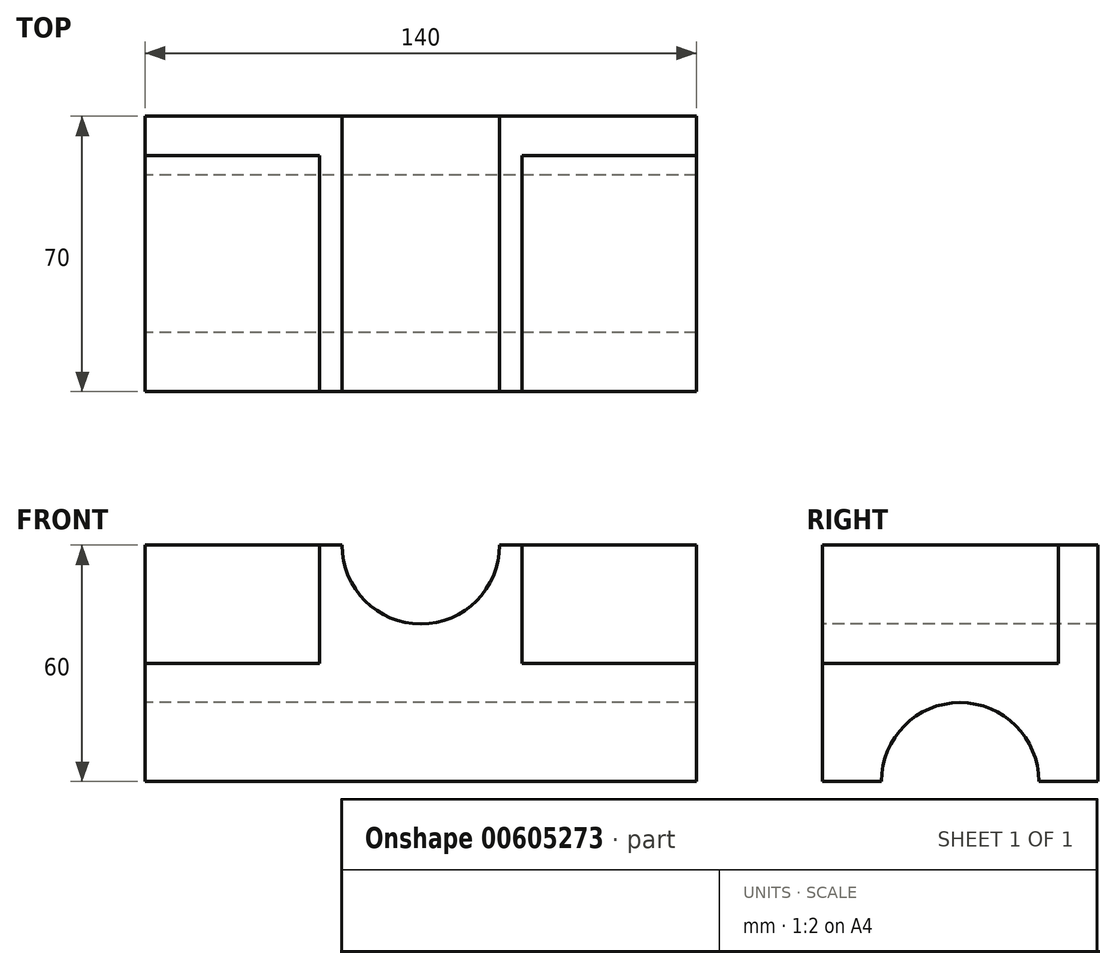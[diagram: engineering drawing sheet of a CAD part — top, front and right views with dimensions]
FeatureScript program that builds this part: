
annotation { "Feature Type Name" : "Feature", "Feature Type Description" : "" }
export const myFeature = defineFeature(function(context is Context, id is Id, definition is map)
    precondition{}
    {
        {
            var Q0;
            Q0=qCreatedBy(makeId("Right.planeOp"),FACE);
            var sketch = newSketch(context, id + "F0", { "sketchPlane" : qUnion([Q0])});
            skLineSegment(sketch, "E0", {"start": v(0, 30) * mm, "end": v(0, 0) * mm});
            skLineSegment(sketch, "E1", {"start": v(0, 0) * mm, "end": v(-60, 0) * mm});
            skLineSegment(sketch, "E2", {"start": v(-60, 0) * mm, "end": v(-60, -30) * mm});
            skLineSegment(sketch, "E3", {"start": v(-60, -30) * mm, "end": v(10, -30) * mm, "construction": true});
            skLineSegment(sketch, "E4", {"start": v(10, -30) * mm, "end": v(10, 30) * mm});
            skLineSegment(sketch, "E5", {"start": v(10, 30) * mm, "end": v(0, 30) * mm});
            skArc(sketch, "E6", {"start": v(-45, -30) * mm, "mid": v(-25, -10) * mm, "end": v(-5, -30) * mm});
            skLineSegment(sketch, "E7", {"start": v(-5, -30) * mm, "end": v(0, -30) * mm});
            skLineSegment(sketch, "E8", {"start": v(-60, -30) * mm, "end": v(-45, -30) * mm});
            skLineSegment(sketch, "E9", {"start": v(-5, -30) * mm, "end": v(10, -30) * mm});
            skSolve(sketch);
        }
        {
            var Q0;
            Q0 = qSketchRegion(id + "F0", true);
            extrude(context, id + "F1", {"entities" : qUnion([Q0]), "endBound" : BoundingType.SYMMETRIC, "depth" : 140 * mm, "offsetDistance" : 25 * mm});
        }
        {
            var Q0;
            Q0=makeQuery(id+"F1.opExtrude","SWEPT_FACE",FACE,{"disambiguationData":[OSD([sQuery(id+"F0.wireOp",EDGE,"E0")])]});
            var sketch = newSketch(context, id + "F2", { "sketchPlane" : qUnion([Q0])});
            skLineSegment(sketch, "E10.bottom", {"start": v(25.7, 0) * mm, "end": v(0, 0) * mm});
            skLineSegment(sketch, "E10.top", {"start": v(25.7, 30) * mm, "end": v(0, 30) * mm});
            skLineSegment(sketch, "E10.left", {"start": v(25.7, 0) * mm, "end": v(25.7, 30) * mm});
            skLineSegment(sketch, "E10.right", {"start": v(0, 0) * mm, "end": v(0, 30) * mm});
            skSolve(sketch);
        }
        {
            var Q0;
            Q0 = qSketchRegion(id + "F2", true);
            extrude(context, id + "F3", {"entities" : qUnion([Q0]), "operationType" : NewBodyOperationType.ADD, "depth" : 60 * mm, "offsetDistance" : 25 * mm});
        }
        {
            var Q0;
            Q0=makeQuery(id+"F1.opExtrude","SWEPT_BODY",BODY,{"disambiguationData":[OSD([sQuery(id+"F0.wireOp",EDGE,"E0"),sQuery(id+"F0.wireOp",EDGE,"E1"),sQuery(id+"F0.wireOp",EDGE,"E2"),sQuery(id+"F0.wireOp",EDGE,"E4"),sQuery(id+"F0.wireOp",EDGE,"E5"),sQuery(id+"F0.wireOp",EDGE,"E6"),sQuery(id+"F0.wireOp",EDGE,"E8"),sQuery(id+"F0.wireOp",EDGE,"E9")])]});
            var Q1;
            Q1=qCreatedBy(makeId("Right.planeOp"),FACE);
            mirror(context, id + "F4", {"operationType" : NewBodyOperationType.ADD, "entities" : qUnion([Q0]), "mirrorPlane" : qUnion([Q1])});
        }
        {
            var Q0;
            {var subQ0=makeQuery(id+"F3.boolean.opBoolean","MERGE",FACE,{"derivedFrom":[makeQuery(id+"F1.opExtrude","SWEPT_FACE",FACE,{"disambiguationData":[OSD([sQuery(id+"F0.wireOp",EDGE,"E2")])]}),makeQuery(id+"F3.opExtrude","CAP_FACE",FACE,{"disambiguationData":[OSD([sQuery(id+"F2.wireOp",EDGE,"E10.bottom"),sQuery(id+"F2.wireOp",EDGE,"E10.top"),sQuery(id+"F2.wireOp",EDGE,"E10.left"),sQuery(id+"F2.wireOp",EDGE,"E10.right")])],"isStart":false})]});Q0=makeQuery(id+"F4.boolean.opBoolean","MERGE",FACE,{"derivedFrom":[subQ0,makeQuery(id+"F4.opPattern","COPY",FACE,{"derivedFrom":subQ0,"instanceName":"1"})]});}
            var sketch = newSketch(context, id + "F5", { "sketchPlane" : qUnion([Q0])});
            skArc(sketch, "E11", {"start": v(-20, 30) * mm, "mid": v(0, 10) * mm, "end": v(20, 30) * mm});
            skSolve(sketch);
        }
        {
            var Q0;
            Q0 = qSketchRegion(id + "F5", true);
            var Q1;
            {var subQ0=sQuery(id+"F5.wireOp",EDGE,"E11");Q1=makeQuery(id+"F5.imprint","IMPRINT",FACE,{"disambiguationData":[TD([[makeQuery(id+"F5.imprint","IMPRINT",EDGE,{"derivedFrom":subQ0}),1.0]])]});}
            extrude(context, id + "F6", {"entities" : qUnion([Q0, Q1]), "operationType" : NewBodyOperationType.REMOVE, "endBound" : BoundingType.THROUGH_ALL, "oppositeDirection" : true, "depth" : 25 * mm, "offsetDistance" : 25 * mm});
        }
    });
